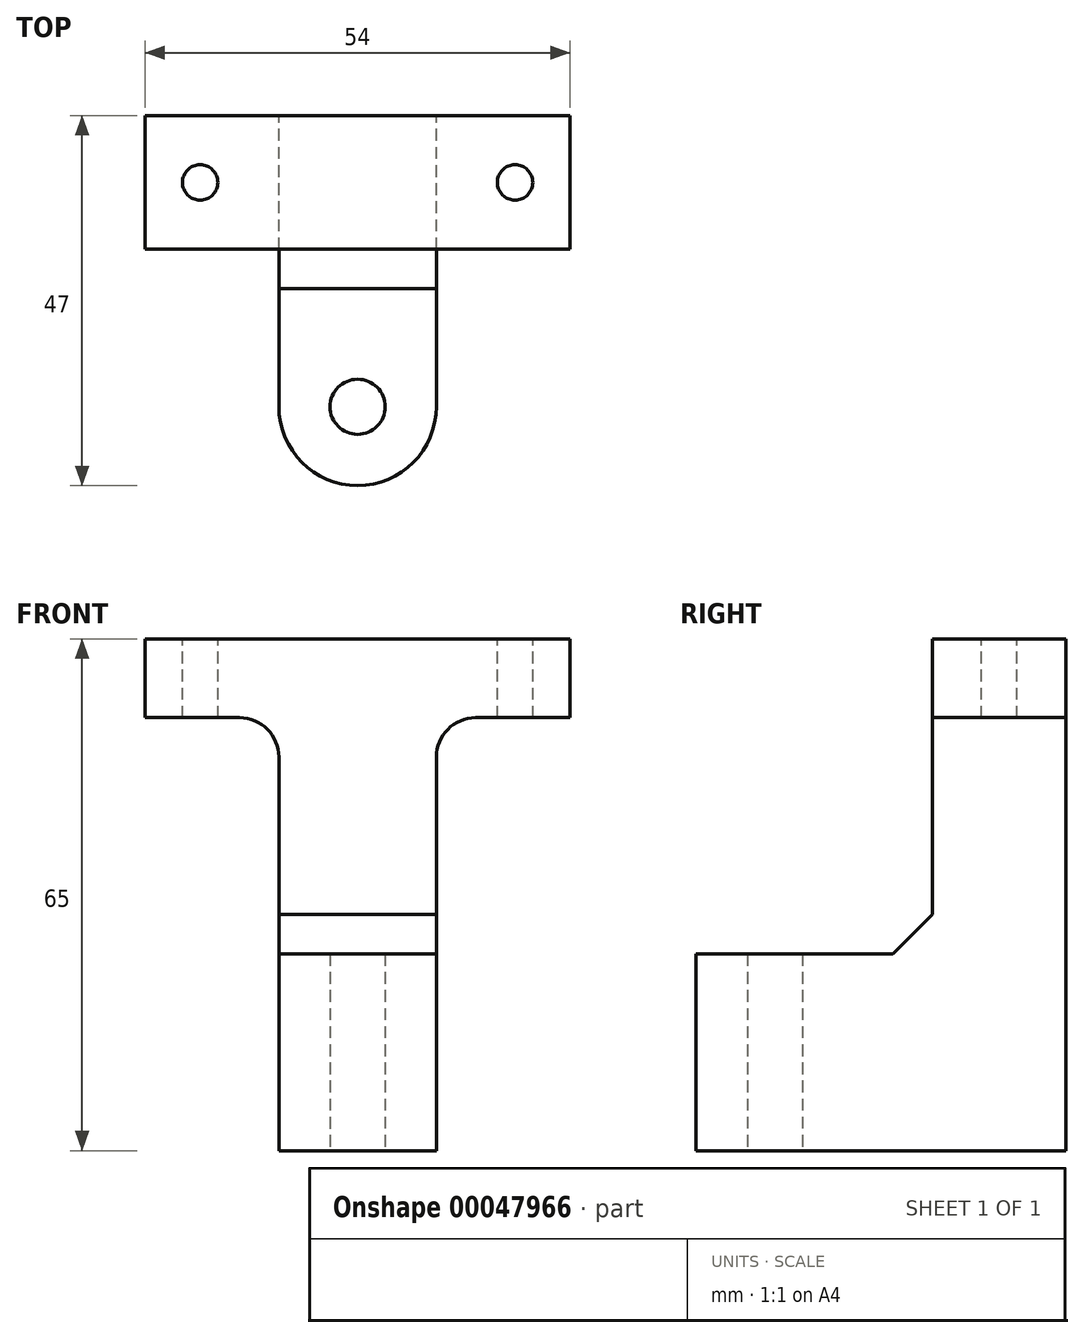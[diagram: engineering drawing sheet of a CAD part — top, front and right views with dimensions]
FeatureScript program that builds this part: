
annotation { "Feature Type Name" : "Feature", "Feature Type Description" : "" }
export const myFeature = defineFeature(function(context is Context, id is Id, definition is map)
    precondition{}
    {
        {
            var Q0;
            Q0=qCreatedBy(makeId("Front.planeOp"),FACE);
            var sketch = newSketch(context, id + "F0", { "sketchPlane" : qUnion([Q0])});
            skLineSegment(sketch, "E0", {"start": v(-27, 40) * mm, "end": v(27, 40) * mm});
            skLineSegment(sketch, "E1", {"start": v(27, 40) * mm, "end": v(27, 30) * mm});
            skLineSegment(sketch, "E2", {"start": v(27, 30) * mm, "end": v(10, 30) * mm});
            skLineSegment(sketch, "E3", {"start": v(10, 30) * mm, "end": v(10, -25) * mm});
            skLineSegment(sketch, "E4", {"start": v(10, -25) * mm, "end": v(-10, -25) * mm});
            skLineSegment(sketch, "E5", {"start": v(-10, -25) * mm, "end": v(-10, 30) * mm});
            skLineSegment(sketch, "E6", {"start": v(-10, 30) * mm, "end": v(-27, 30) * mm});
            skLineSegment(sketch, "E7", {"start": v(-27, 30) * mm, "end": v(-27, 40) * mm});
            skLineSegment(sketch, "E8", {"start": v(0, 0) * mm, "end": v(0, -25) * mm, "construction": true});
            skLineSegment(sketch, "E9", {"start": v(-10, 0) * mm, "end": v(10, 0) * mm, "construction": true});
            skSolve(sketch);
        }
        {
            var Q0;
            Q0 = qSketchRegion(id + "F0", true);
            extrude(context, id + "F1", {"entities" : qUnion([Q0]), "depth" : 47 * mm});
        }
        {
            var Q0;
            Q0=makeQuery(id+"F1.opExtrude","SWEPT_FACE",FACE,{"disambiguationData":[OSD([sQuery(id+"F0.wireOp",EDGE,"E4")])]});
            var sketch = newSketch(context, id + "F2", { "sketchPlane" : qUnion([Q0])});
            skPoint(sketch, "E10", {"position": v(0, 37) * mm});
            skCircle(sketch, "E11", {"center": v(0, 37) * mm, "radius": 9.5 * mm});
            skCircle(sketch, "E12", {"center": v(0, 37) * mm, "radius": 16 * mm});
            skCircle(sketch, "E13", {"center": v(0, 15) * mm, "radius": 38 * mm});
            skCircle(sketch, "E14", {"center": v(0, 15) * mm, "radius": 28.5 * mm});
            skCircle(sketch, "E15.cCircle", {"center": v(0, 37) * mm, "radius": 5.5 * mm, "construction": true});
            skLineSegment(sketch, "E15.0", {"start": v(-4.76, 39.75) * mm, "end": v(0, 42.5) * mm});
            skLineSegment(sketch, "E15.1", {"start": v(0, 42.5) * mm, "end": v(4.76, 39.75) * mm});
            skLineSegment(sketch, "E15.2", {"start": v(4.76, 39.75) * mm, "end": v(4.76, 34.25) * mm});
            skLineSegment(sketch, "E15.3", {"start": v(4.76, 34.25) * mm, "end": v(0, 31.5) * mm});
            skLineSegment(sketch, "E15.4", {"start": v(0, 31.5) * mm, "end": v(-4.76, 34.25) * mm});
            skLineSegment(sketch, "E15.5", {"start": v(-4.76, 34.25) * mm, "end": v(-4.76, 39.75) * mm});
            skLineSegment(sketch, "E16", {"start": v(0, 53) * mm, "end": v(0, 43.5) * mm});
            skPoint(sketch, "E16.startSnap0", {"position": v(0, 47) * mm});
            skSolve(sketch);
        }
        {
            var Q0;
            Q0=sQuery(id+"F2.wireOp",VERTEX,"E10");
            var Q1;
            Q1=makeQuery(id+"F1.opExtrude","SWEPT_BODY",BODY,{"disambiguationData":[OSD([sQuery(id+"F0.wireOp",EDGE,"E0"),sQuery(id+"F0.wireOp",EDGE,"E1"),sQuery(id+"F0.wireOp",EDGE,"E2"),sQuery(id+"F0.wireOp",EDGE,"E3"),sQuery(id+"F0.wireOp",EDGE,"E4"),sQuery(id+"F0.wireOp",EDGE,"E5"),sQuery(id+"F0.wireOp",EDGE,"E6"),sQuery(id+"F0.wireOp",EDGE,"E7")])]});
            hole(context, id + "F3", {"style" : HoleStyle.SIMPLE, "holeDiameter" : 7 * mm, "endStyle" : HoleEndStyle.THROUGH, "locations" : qUnion([Q0]), "scope" : qUnion([Q1])});
        }
        {
            var Q0;
            Q0=qCreatedBy(makeId("Top.planeOp"),FACE);
            var sketch = newSketch(context, id + "F4", { "sketchPlane" : qUnion([Q0])});
            skLineSegment(sketch, "E17.bottom", {"start": v(27, -47) * mm, "end": v(-27, -47) * mm});
            skLineSegment(sketch, "E17.top", {"start": v(27, -17) * mm, "end": v(-27, -17) * mm});
            skLineSegment(sketch, "E17.left", {"start": v(27, -47) * mm, "end": v(27, -17) * mm});
            skLineSegment(sketch, "E17.right", {"start": v(-27, -47) * mm, "end": v(-27, -17) * mm});
            skSolve(sketch);
        }
        {
            var Q0;
            Q0 = qSketchRegion(id + "F4", true);
            extrude(context, id + "F5", {"entities" : qUnion([Q0]), "operationType" : NewBodyOperationType.REMOVE, "endBound" : BoundingType.THROUGH_ALL, "depth" : 25 * mm});
        }
        {
            var Q0;
            Q0=makeQuery(id+"F1.opExtrude","CAP_EDGE",EDGE,{"disambiguationData":[OSD([sQuery(id+"F0.wireOp",EDGE,"E5")])],"isStart":false});
            var Q1;
            Q1=makeQuery(id+"F1.opExtrude","CAP_EDGE",EDGE,{"disambiguationData":[OSD([sQuery(id+"F0.wireOp",EDGE,"E3")])],"isStart":false});
            fillet(context, id + "F6", {"entities" : qUnion([Q0, Q1]), "radius" : 10 * mm, "tangentPropagation" : true, "allowEdgeOverflow" : false});
        }
        {
            var Q0;
            Q0=makeQuery(id+"F5.boolean.opBoolean","COPY",FACE,{"derivedFrom":makeQuery(id+"F5.opExtrude","SWEPT_FACE",FACE,{"disambiguationData":[OSD([sQuery(id+"F4.wireOp",EDGE,"E17.top")])]})});
            var sketch = newSketch(context, id + "F7", { "sketchPlane" : qUnion([Q0])});
            skLineSegment(sketch, "E18.bottom", {"start": v(-27, 30) * mm, "end": v(27, 30) * mm});
            skLineSegment(sketch, "E18.top", {"start": v(-27, 40) * mm, "end": v(27, 40) * mm});
            skLineSegment(sketch, "E18.left", {"start": v(-27, 30) * mm, "end": v(-27, 40) * mm});
            skLineSegment(sketch, "E18.right", {"start": v(27, 30) * mm, "end": v(27, 40) * mm});
            skSolve(sketch);
        }
        {
            var Q0;
            Q0=makeQuery(id+"F1.opExtrude","SWEPT_EDGE",EDGE,{"disambiguationData":[OSD([sQuery(id+"F0.wireOp",EDGE,"E2"),sQuery(id+"F0.wireOp",EDGE,"E3")])]});
            var Q1;
            Q1=makeQuery(id+"F1.opExtrude","SWEPT_EDGE",EDGE,{"disambiguationData":[OSD([sQuery(id+"F0.wireOp",EDGE,"E5"),sQuery(id+"F0.wireOp",EDGE,"E6")])]});
            fillet(context, id + "F8", {"entities" : qUnion([Q0, Q1]), "radius" : 5 * mm, "tangentPropagation" : true, "allowEdgeOverflow" : false});
        }
        {
            var Q0;
            Q0=makeQuery(id+"FD3dBrjHjbZUdcs_1.boolean.opBoolean","MERGE",FACE,{"derivedFrom":[makeQuery(id+"F1.opExtrude","SWEPT_FACE",FACE,{"disambiguationData":[OSD([sQuery(id+"F0.wireOp",EDGE,"E0")])]}),makeQuery(id+"FD3dBrjHjbZUdcs_1.opExtrude","SWEPT_FACE",FACE,{"disambiguationData":[OSD([sQuery(id+"F7.wireOp",EDGE,"E18.top")])]})]});
            var sketch = newSketch(context, id + "F9", { "sketchPlane" : qUnion([Q0])});
            skPoint(sketch, "E19", {"position": v(-20, -8.5) * mm});
            skPoint(sketch, "E20", {"position": v(20, -8.5) * mm});
            skLineSegment(sketch, "E21", {"start": v(-27, -8.5) * mm, "end": v(-20, -8.5) * mm});
            skSolve(sketch);
        }
        {
            var Q0;
            Q0=sQuery(id+"F9.wireOp",VERTEX,"E19");
            var Q1;
            Q1=sQuery(id+"F9.wireOp",VERTEX,"E20");
            var Q2;
            Q2=makeQuery(id+"F1.opExtrude","SWEPT_BODY",BODY,{"disambiguationData":[OSD([sQuery(id+"F0.wireOp",EDGE,"E0"),sQuery(id+"F0.wireOp",EDGE,"E1"),sQuery(id+"F0.wireOp",EDGE,"E2"),sQuery(id+"F0.wireOp",EDGE,"E3"),sQuery(id+"F0.wireOp",EDGE,"E4"),sQuery(id+"F0.wireOp",EDGE,"E5"),sQuery(id+"F0.wireOp",EDGE,"E6"),sQuery(id+"F0.wireOp",EDGE,"E7")])]});
            hole(context, id + "F10", {"style" : HoleStyle.SIMPLE, "holeDiameter" : 4.5 * mm, "endStyle" : HoleEndStyle.THROUGH, "locations" : qUnion([Q0, Q1]), "scope" : qUnion([Q2])});
        }
        {
            var Q0;
            Q0=makeQuery(id+"F5.boolean.opBoolean","COPY",EDGE,{"derivedFrom":makeQuery(id+"F5.opExtrude","CAP_EDGE",EDGE,{"disambiguationData":[OSD([sQuery(id+"F4.wireOp",EDGE,"E17.top")])],"isStart":true})});
            chamfer(context, id + "F11", {"entities" : qUnion([Q0]), "width" : 5 * mm, "tangentPropagation" : true});
        }
    });
